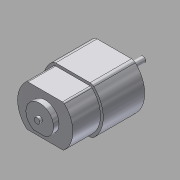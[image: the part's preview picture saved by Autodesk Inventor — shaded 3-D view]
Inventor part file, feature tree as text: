
AUTODESK INVENTOR PART (.ipt)
format: ipt  version: 2015 (Build 190159000, 159)  size: 139,264 bytes
history: native  units: in
note: dims shown in document units (in); Inventor stores cm internally (conversion verified against a paired STEP export)
features: sketch x5, other x3
ambient origin geometry x8: Origin, YZ Plane, XZ Plane, XY Plane, X Axis, Y Axis, Z Axis, Center Point
bodies: Solid1 (feature_tree)
feature tree (8):
  other  "motor_MIR3.ipt"
  other  "Solid1::motor_MIR3.ipt"
  other  "TaggingFeature1"
  sketch  "Sketch1"  dims[d0=0.3937in]
  sketch  "Sketch2"
  sketch  "Sketch3"
  sketch  "Sketch4"
  sketch  "Sketch5"
